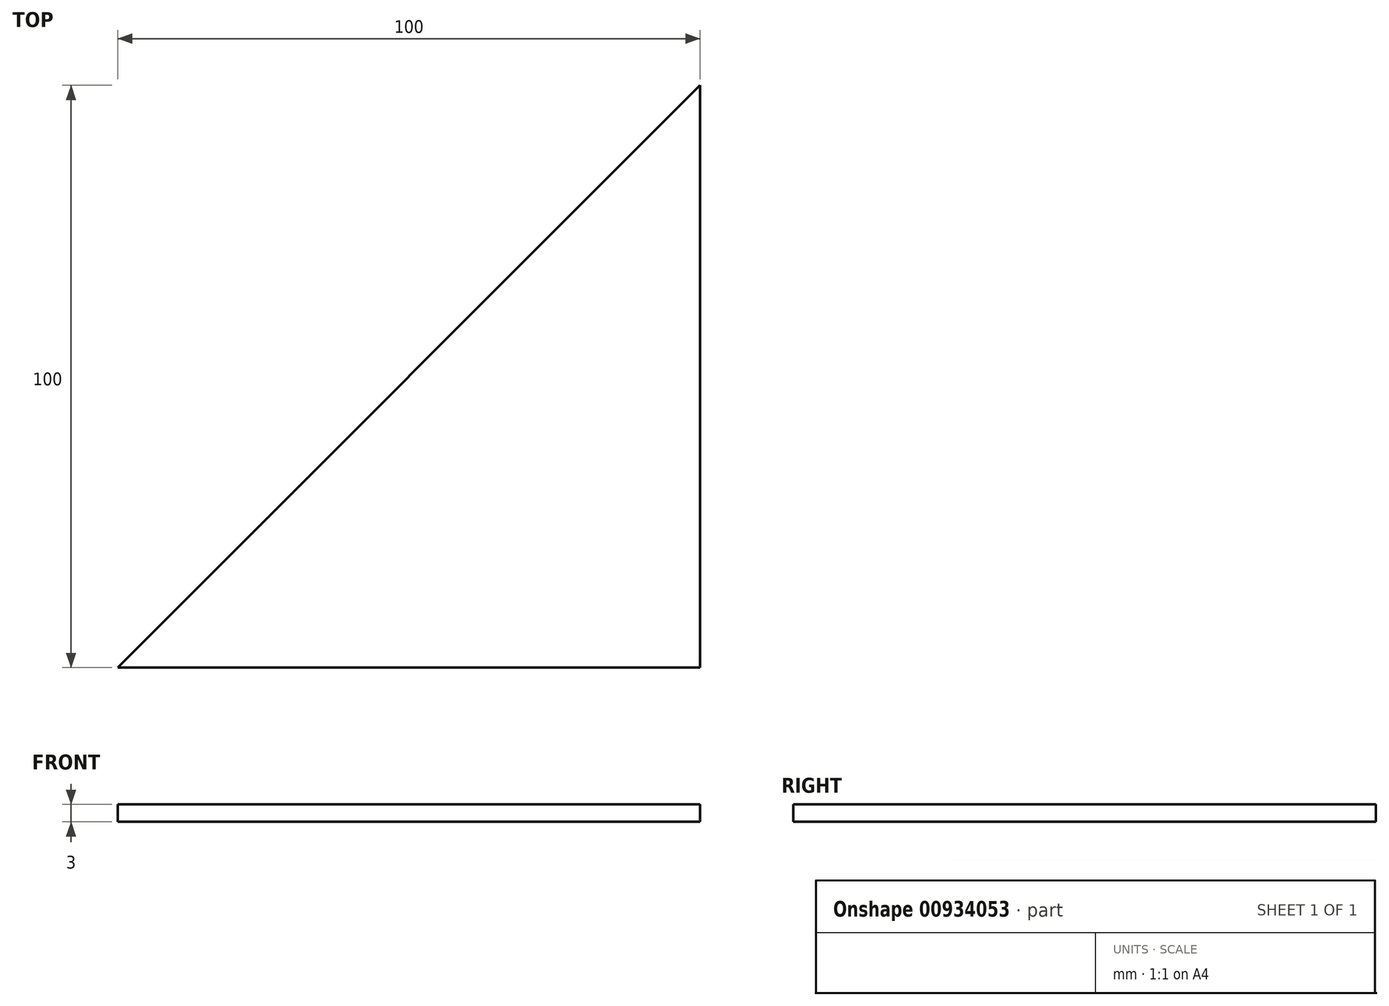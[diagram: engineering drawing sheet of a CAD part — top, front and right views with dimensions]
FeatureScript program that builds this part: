
annotation { "Feature Type Name" : "Feature", "Feature Type Description" : "" }
export const myFeature = defineFeature(function(context is Context, id is Id, definition is map)
    precondition{}
    {
        {
            var Q0;
            Q0=qCreatedBy(makeId("Top.planeOp"),FACE);
            var sketch = newSketch(context, id + "F0", { "sketchPlane" : qUnion([Q0])});
            skLineSegment(sketch, "E0", {"start": v(0, 0) * mm, "end": v(-100, 0) * mm});
            skLineSegment(sketch, "E1", {"start": v(-100, 0) * mm, "end": v(0, 100) * mm});
            skLineSegment(sketch, "E2", {"start": v(0, 100) * mm, "end": v(0, 0) * mm});
            skSolve(sketch);
        }
        {
            var Q0;
            Q0 = qSketchRegion(id + "F0", true);
            extrude(context, id + "F1", {"entities" : qUnion([Q0]), "depth" : 3 * mm, "offsetDistance" : 25 * mm});
        }
        {
            var Q0;
            Q0=qCreatedBy(makeId("Top.planeOp"),FACE);
            cPlane(context, id + "F2", {"entities" : qUnion([Q0]), "cplaneType" : CPlaneType.OFFSET, "offset" : 50 * mm, "width" : 150 * mm, "height" : 150 * mm});
        }
    });
